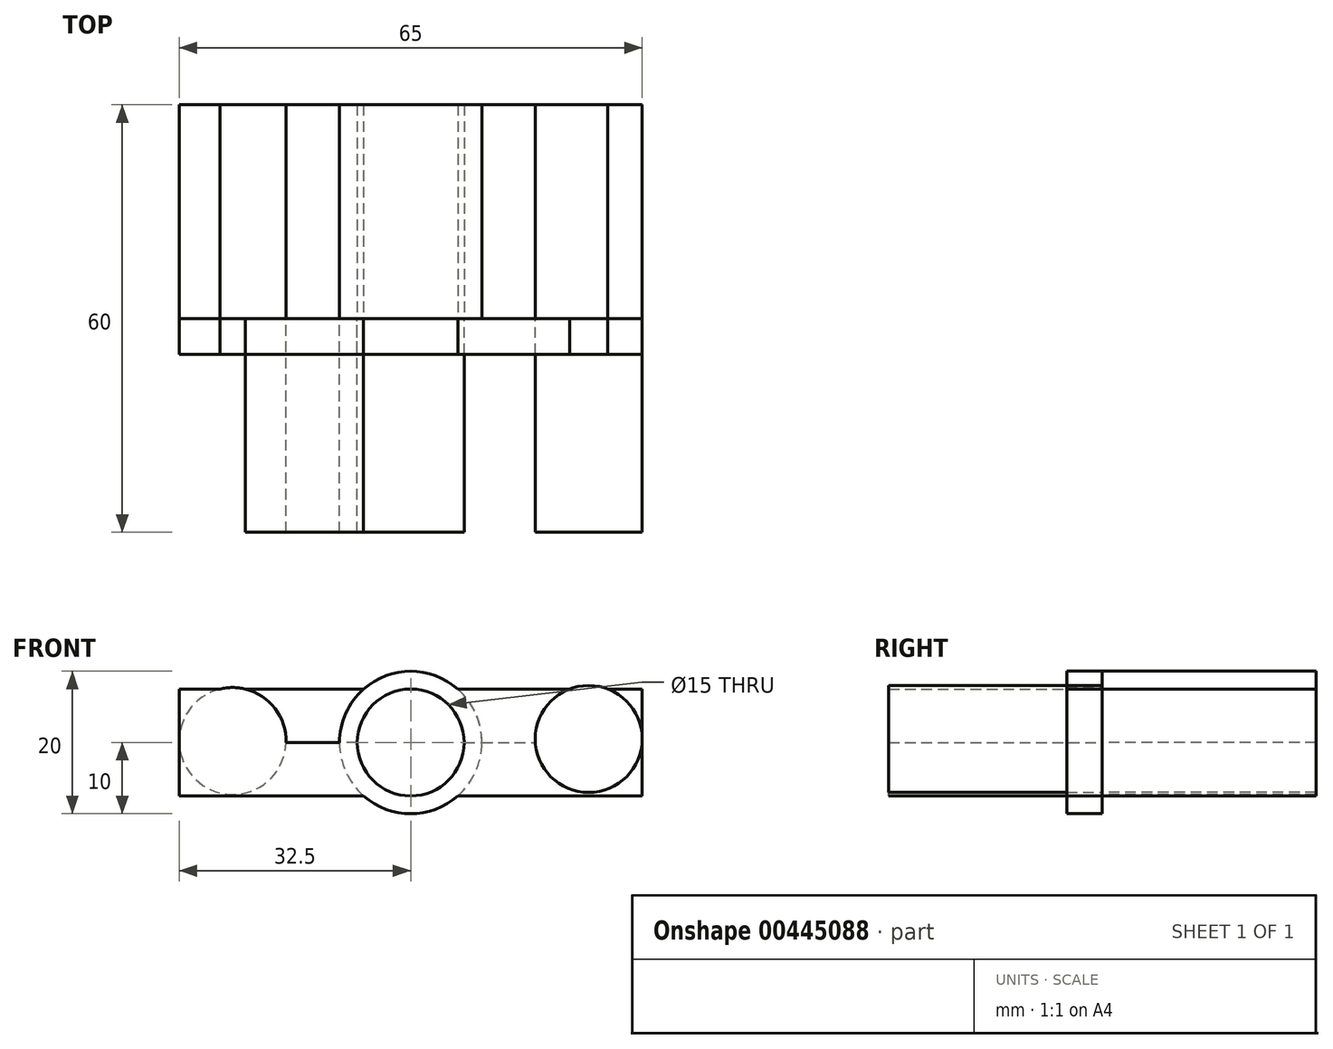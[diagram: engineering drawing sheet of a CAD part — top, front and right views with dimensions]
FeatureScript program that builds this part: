
annotation { "Feature Type Name" : "Feature", "Feature Type Description" : "" }
export const myFeature = defineFeature(function(context is Context, id is Id, definition is map)
    precondition{}
    {
        {
            var Q0;
            Q0=qCreatedBy(makeId("Front.planeOp"),FACE);
            var sketch = newSketch(context, id + "F0", { "sketchPlane" : qUnion([Q0])});
            skLineSegment(sketch, "E0.bottom", {"start": v(-32.5, 7.5) * mm, "end": v(32.5, 7.5) * mm});
            skLineSegment(sketch, "E0.top", {"start": v(-32.5, -7.5) * mm, "end": v(32.5, -7.5) * mm});
            skLineSegment(sketch, "E0.left", {"start": v(-32.5, 7.5) * mm, "end": v(-32.5, -7.5) * mm});
            skLineSegment(sketch, "E0.right", {"start": v(32.5, 7.5) * mm, "end": v(32.5, -7.5) * mm});
            skPoint(sketch, "E0.middle", {"position": v(0, 0) * mm});
            skCircle(sketch, "E1", {"center": v(0, 0) * mm, "radius": 7.5 * mm});
            skLineSegment(sketch, "E2", {"start": v(-7.5, 0) * mm, "end": v(-17.5, 0) * mm});
            skLineSegment(sketch, "E3", {"start": v(0, 0) * mm, "end": v(7.5, 0) * mm});
            skLineSegment(sketch, "E4", {"start": v(7.5, 0) * mm, "end": v(17.5, 0) * mm});
            skCircle(sketch, "E5", {"center": v(-25, 0.21) * mm, "radius": 7.5 * mm});
            skPoint(sketch, "E5.second.point", {"position": v(-32.5, 0) * mm});
            skPoint(sketch, "E5.third.point", {"position": v(-32.21, 2.26) * mm});
            skCircle(sketch, "E6", {"center": v(24.98, 0.5) * mm, "radius": 7.5 * mm});
            skPoint(sketch, "E6.first.point", {"position": v(32.47, 0) * mm});
            skPoint(sketch, "E6.third.point", {"position": v(31.08, 4.86) * mm});
            skCircle(sketch, "E7", {"center": v(0, 0) * mm, "radius": 10 * mm});
            skSolve(sketch);
        }
        {
            var Q0;
            Q0 = qSketchRegion(id + "F0", true);
            extrude(context, id + "F1", {"entities" : qUnion([Q0]), "depth" : 5 * mm});
        }
        {
            var Q0;
            {var subQ0=sQuery(id+"F0.wireOp",EDGE,"E5");var subQ1=sQuery(id+"F0.wireOp",EDGE,"E0.bottom");var subQ2=makeQuery(id+"F0.imprint","INTERSECT",VERTEX,{"disambiguationData":[OD(0.0)],"derivedFrom":[subQ1,subQ0]});Q0=makeQuery(id+"F0.imprint","IMPRINT",FACE,{"disambiguationData":[TD([[makeQuery(id+"F0.imprint","IMPRINT",EDGE,{"disambiguationData":[TD([[subQ2,-1.0]])],"derivedFrom":subQ1}),1.0]])]});}
            var Q1;
            {var subQ0=sQuery(id+"F0.wireOp",EDGE,"E6");var subQ1=sQuery(id+"F0.wireOp",EDGE,"E0.bottom");var subQ2=makeQuery(id+"F0.imprint","INTERSECT",VERTEX,{"disambiguationData":[OD(0.0)],"derivedFrom":[subQ1,subQ0]});Q1=makeQuery(id+"F0.imprint","IMPRINT",FACE,{"disambiguationData":[TD([[makeQuery(id+"F0.imprint","IMPRINT",EDGE,{"disambiguationData":[TD([[subQ2,-1.0]])],"derivedFrom":subQ1}),1.0]])]});}
            var Q2;
            {var subQ0=sQuery(id+"F0.wireOp",EDGE,"E5");var subQ1=sQuery(id+"F0.wireOp",EDGE,"E0.bottom");var subQ2=makeQuery(id+"F0.imprint","INTERSECT",VERTEX,{"disambiguationData":[OD(0.0)],"derivedFrom":[subQ1,subQ0]});Q2=makeQuery(id+"F0.imprint","IMPRINT",FACE,{"disambiguationData":[TD([[makeQuery(id+"F0.imprint","IMPRINT",EDGE,{"disambiguationData":[TD([[subQ2,-1.0]])],"derivedFrom":subQ1}),-1.0]])]});}
            var Q3;
            {var subQ0=sQuery(id+"F0.wireOp",EDGE,"E6");var subQ1=sQuery(id+"F0.wireOp",EDGE,"E0.bottom");var subQ2=makeQuery(id+"F0.imprint","INTERSECT",VERTEX,{"disambiguationData":[OD(0.0)],"derivedFrom":[subQ1,subQ0]});Q3=makeQuery(id+"F0.imprint","IMPRINT",FACE,{"disambiguationData":[TD([[makeQuery(id+"F0.imprint","IMPRINT",EDGE,{"disambiguationData":[TD([[subQ2,-1.0]])],"derivedFrom":subQ1}),-1.0]])]});}
            var Q4;
            {var subQ0=sQuery(id+"F0.wireOp",EDGE,"E1");var subQ1=makeQuery(id+"F0.imprint","INTERSECT",VERTEX,{"derivedFrom":[subQ0,sQuery(id+"F0.wireOp",EDGE,"E4")]});Q4=makeQuery(id+"F0.imprint","IMPRINT",FACE,{"disambiguationData":[TD([[makeQuery(id+"F0.imprint","IMPRINT",EDGE,{"disambiguationData":[TD([[subQ1,-1.0]])],"derivedFrom":subQ0}),1.0]])]});}
            extrude(context, id + "F2", {"entities" : qUnion([Q0, Q1, Q2, Q3, Q4]), "depth" : 30 * mm});
        }
        {
            var Q0;
            {var subQ0=sQuery(id+"F0.wireOp",EDGE,"E7");var subQ1=sQuery(id+"F0.wireOp",EDGE,"E0.bottom");var subQ2=makeQuery(id+"F0.imprint","INTERSECT",VERTEX,{"disambiguationData":[OD(1.0)],"derivedFrom":[subQ1,subQ0]});Q0=makeQuery(id+"F0.imprint","IMPRINT",FACE,{"disambiguationData":[TD([[makeQuery(id+"F0.imprint","IMPRINT",EDGE,{"disambiguationData":[TD([[subQ2,1.0]])],"derivedFrom":subQ1}),-1.0]])]});}
            var Q1;
            {var subQ0=sQuery(id+"F0.wireOp",EDGE,"E1");var subQ1=makeQuery(id+"F0.imprint","INTERSECT",VERTEX,{"derivedFrom":[subQ0,sQuery(id+"F0.wireOp",EDGE,"E4")]});Q1=makeQuery(id+"F0.imprint","IMPRINT",FACE,{"disambiguationData":[TD([[makeQuery(id+"F0.imprint","IMPRINT",EDGE,{"disambiguationData":[TD([[subQ1,-1.0]])],"derivedFrom":subQ0}),1.0]])]});}
            var Q2;
            {var subQ0=sQuery(id+"F0.wireOp",EDGE,"E7");var subQ1=sQuery(id+"F0.wireOp",EDGE,"E0.bottom");var subQ2=makeQuery(id+"F0.imprint","INTERSECT",VERTEX,{"disambiguationData":[OD(0.0)],"derivedFrom":[subQ1,subQ0]});Q2=makeQuery(id+"F0.imprint","IMPRINT",FACE,{"disambiguationData":[TD([[makeQuery(id+"F0.imprint","IMPRINT",EDGE,{"disambiguationData":[TD([[subQ2,-1.0]])],"derivedFrom":subQ1}),1.0]])]});}
            var Q3;
            {var subQ0=sQuery(id+"F0.wireOp",EDGE,"E7");var subQ1=sQuery(id+"F0.wireOp",EDGE,"E0.bottom");var subQ2=makeQuery(id+"F0.imprint","INTERSECT",VERTEX,{"disambiguationData":[OD(0.0)],"derivedFrom":[subQ1,subQ0]});Q3=makeQuery(id+"F0.imprint","IMPRINT",FACE,{"disambiguationData":[TD([[makeQuery(id+"F0.imprint","IMPRINT",EDGE,{"disambiguationData":[TD([[subQ2,-1.0]])],"derivedFrom":subQ1}),-1.0]])]});}
            var Q4;
            {var subQ0=sQuery(id+"F0.wireOp",EDGE,"E7");var subQ1=sQuery(id+"F0.wireOp",EDGE,"E0.top");var subQ2=makeQuery(id+"F0.imprint","INTERSECT",VERTEX,{"disambiguationData":[OD(0.0)],"derivedFrom":[subQ1,subQ0]});Q4=makeQuery(id+"F0.imprint","IMPRINT",FACE,{"disambiguationData":[TD([[makeQuery(id+"F0.imprint","IMPRINT",EDGE,{"disambiguationData":[TD([[subQ2,-1.0]])],"derivedFrom":subQ1}),1.0]])]});}
            var Q5;
            {var subQ0=sQuery(id+"F0.wireOp",EDGE,"E7");var subQ1=sQuery(id+"F0.wireOp",EDGE,"E0.top");var subQ2=makeQuery(id+"F0.imprint","INTERSECT",VERTEX,{"disambiguationData":[OD(0.0)],"derivedFrom":[subQ1,subQ0]});Q5=makeQuery(id+"F0.imprint","IMPRINT",FACE,{"disambiguationData":[TD([[makeQuery(id+"F0.imprint","IMPRINT",EDGE,{"disambiguationData":[TD([[subQ2,-1.0]])],"derivedFrom":subQ1}),-1.0]])]});}
            var Q6;
            {var subQ0=sQuery(id+"F0.wireOp",EDGE,"E7");var subQ1=sQuery(id+"F0.wireOp",EDGE,"E0.top");var subQ2=makeQuery(id+"F0.imprint","INTERSECT",VERTEX,{"disambiguationData":[OD(1.0)],"derivedFrom":[subQ1,subQ0]});Q6=makeQuery(id+"F0.imprint","IMPRINT",FACE,{"disambiguationData":[TD([[makeQuery(id+"F0.imprint","IMPRINT",EDGE,{"disambiguationData":[TD([[subQ2,1.0]])],"derivedFrom":subQ1}),1.0]])]});}
            extrude(context, id + "F3", {"entities" : qUnion([Q0, Q1, Q2, Q3, Q4, Q5, Q6]), "oppositeDirection" : true, "depth" : 30 * mm});
        }
    });
